# Revit family: Floor_Access_Housing_Heavy_Duty-Zurn-Z1404
name_source: partatom
category: Plumbing Fixtures
units: mm (PartAtom-declared; Revit-internal decimal feet)

## family parameters
Always vertical = Yes
Cut with Voids When Loaded = No
Maintain Annotation Orientation = No
OmniClass Number = 23.45.55.21
OmniClass Title = Drains (Wastes)
Part Type = Normal
Room Calculation Point = No
Round Connector Dimension = Use Radius
Shared = No
Work Plane-Based = No

## types (9) — shared parameters
Assembly Code = D2030400
CW Connection = No
Default Elevation = 20 "
Description = HEAVY-DUTY FLOOR ACCESS HOUSING
HW Connection = No
Main Material = Iron - Zurn - Cast - Painted - Blue
Manufacturer = Zurn Water, LLC
Manufacurer Brand = Zurn
Modified Date = 02/27/2026
Product Documentation Link = https://files.zurn.com
Product Page URL = https://www.zurn.com
Product data url = https://www.bimobject.com
Screw Material = Steel - Zurn - Stainless - Type - 304
URL = www.zurn.com
Vent Connection = No
WFU = 1
Waste Connection = Yes
zero-valued in all types: CWFU, HWFU

## per-type parameters (varying)
| type | Approx Weight | Body Height_E | Connector Radius | Frame & Cover Material | Frame Outer Dim_C | Pipe Size_A Inside Diameter | Pipe Size_A Nominal Diameter | Pipe Size_A Outer Diameter | Type Comments |
| Z1404 3 Inch | 3.00 lb | 0.875 " | 1.5 " | Iron - Zurn - Cast - Painted - Blue | 6.125 " | 3.068 " | 3 " | 3.5 " | Z1404-3 Inch-Slip Joint Outlet |
| Z1404 4 Inch | 4.00 lb | 0.875 " | 2 " | Iron - Zurn - Cast - Painted - Blue | 7.25 " | 4.026 " | 4 " | 4.5 " | Z1404-4 Inch-Slip Joint Outlet |
| Z1404 6 Inch | 8.00 lb | 0.875 " | 3 " | Iron - Zurn - Cast - Painted - Blue | 9.25 " | 6.065 " | 6 " | 6.625 " | Z1404-6 Inch-Slip Joint Outlet |
| ZN1404 3 Inch | 3.00 lb | 0.375 " | 1.5 " | Bronze - Zurn - Polished Nickel | 6.125 " | 3.068 " | 3 " | 3.5 " | ZN1404-3 Inch-Slip Joint Outlet |
| ZN1404 4 Inch | 4.00 lb | 0.375 " | 2 " | Bronze - Zurn - Polished Nickel | 7.25 " | 4.026 " | 4 " | 4.5 " | ZN1404-4 Inch-Slip Joint Outlet |
| ZN1404 6 Inch | 8.00 lb | 0.375 " | 3 " | Bronze - Zurn - Polished Nickel | 9.25 " | 6.065 " | 6 " | 6.625 " | ZN1404-6 Inch-Slip Joint Outlet |
| ZS1404 3 Inch | 3.00 lb | 1.063 " | 1.5 " | Steel - Zurn - Stainless - Type - 304 | 6.125 " | 3.068 " | 3 " | 3.5 " | ZS1404-3 Inch-Slip Joint Outlet |
| ZS1404 4 Inch | 4.00 lb | 1.063 " | 2 " | Steel - Zurn - Stainless - Type - 304 | 7.25 " | 4.026 " | 4 " | 4.5 " | ZS1404-4 Inch-Slip Joint Outlet |
| ZS1404 6 Inch | 8.00 lb | 1.063 " | 3 " | Steel - Zurn - Stainless - Type - 304 | 9.25 " | 6.065 " | 6 " | 6.625 " | ZS1404-6 Inch-Slip Joint Outlet |

note: column(s) folded — value = type name in every type: Model

## geometry (parser evidence)
native form markers: Blend x6, Sweep x2
no freeform markers — native parametric forms only
